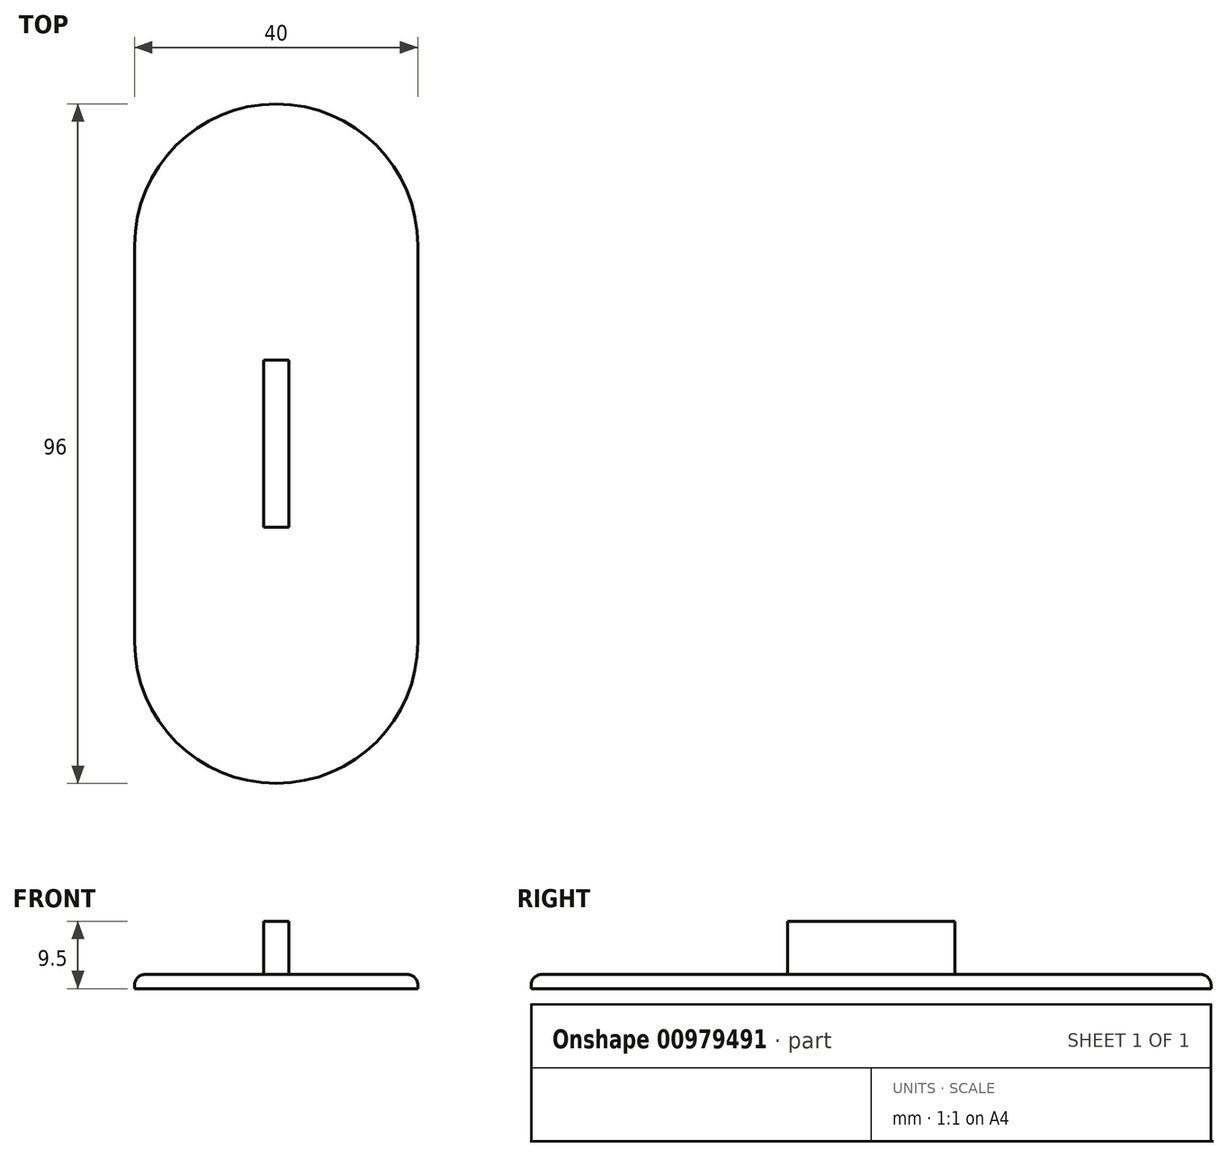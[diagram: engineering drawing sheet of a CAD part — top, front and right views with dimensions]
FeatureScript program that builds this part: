
annotation { "Feature Type Name" : "Feature", "Feature Type Description" : "" }
export const myFeature = defineFeature(function(context is Context, id is Id, definition is map)
    precondition{}
    {
        {
            assignVariable(context, id + "F0", {"name" : "MATE_DEPTH", "anyValue" : 8});
        }
        {
            var Q0;
            Q0=qCreatedBy(makeId("Top.planeOp"),FACE);
            var sketch = newSketch(context, id + "F1", { "sketchPlane" : qUnion([Q0])});
            skLineSegment(sketch, "E0.bottom", {"start": v(0, 0) * mm, "end": v(-5, 0) * mm});
            skLineSegment(sketch, "E0.top", {"start": v(0, 28) * mm, "end": v(-5, 28) * mm});
            skLineSegment(sketch, "E0.left", {"start": v(0, 0) * mm, "end": v(0, 28) * mm});
            skLineSegment(sketch, "E0.right", {"start": v(-5, 0) * mm, "end": v(-5, 28) * mm});
            skLineSegment(sketch, "E1.MirrorCS", {"start": v(0, 28) * mm, "end": v(5, 28) * mm});
            skLineSegment(sketch, "E2.MirrorCS", {"start": v(5, 0) * mm, "end": v(5, 28) * mm});
            skCircle(sketch, "E3", {"center": v(0, 28) * mm, "radius": 5 * mm});
            skLineSegment(sketch, "E4.MirrorCS", {"start": v(-5, 0) * mm, "end": v(-5, -28) * mm});
            skLineSegment(sketch, "E5.MirrorCS", {"start": v(5, 0) * mm, "end": v(5, -28) * mm});
            skCircle(sketch, "E6.MirrorC", {"center": v(0, -28) * mm, "radius": 5 * mm});
            skSolve(sketch);
        }
        {
            var Q0;
            Q0 = qSketchRegion(id + "F1", true);
            extrude(context, id + "F2", {"entities" : qUnion([Q0]), "depth" : 1 * mm, "offsetDistance" : 25 * mm});
        }
        {
            var Q0;
            Q0=qCreatedBy(makeId("Top.planeOp"),FACE);
            var sketch = newSketch(context, id + "F3", { "sketchPlane" : qUnion([Q0])});
            skArc(sketch, "E7.0", {"start": v(-20, -28) * mm, "mid": v(0, -48) * mm, "end": v(20, -28) * mm});
            skLineSegment(sketch, "E7.1", {"start": v(-20, 28) * mm, "end": v(-20, -28) * mm});
            skArc(sketch, "E7.2", {"start": v(20, 28) * mm, "mid": v(0, 48) * mm, "end": v(-20, 28) * mm});
            skLineSegment(sketch, "E7.3", {"start": v(20, -28) * mm, "end": v(20, 28) * mm});
            skSolve(sketch);
        }
        {
            var Q0;
            Q0 = qSketchRegion(id + "F3", true);
            extrude(context, id + "F4", {"entities" : qUnion([Q0]), "operationType" : NewBodyOperationType.ADD, "depth" : 2 * mm, "offsetDistance" : 25 * mm});
        }
        {
            var Q0;
            Q0=makeQuery(id+"F4.opExtrude","CAP_FACE",FACE,{"disambiguationData":[OSD([sQuery(id+"F3.wireOp",EDGE,"E7.0"),sQuery(id+"F3.wireOp",EDGE,"E7.1"),sQuery(id+"F3.wireOp",EDGE,"E7.2"),sQuery(id+"F3.wireOp",EDGE,"E7.3")])],"isStart":false});
            var sketch = newSketch(context, id + "F5", { "sketchPlane" : qUnion([Q0])});
            skLineSegment(sketch, "E8.bottom", {"start": v(0, 0) * mm, "end": v(-1.8, 0) * mm});
            skLineSegment(sketch, "E8.top", {"start": v(0, 11.8) * mm, "end": v(-1.8, 11.8) * mm});
            skLineSegment(sketch, "E8.left", {"start": v(0, 0) * mm, "end": v(0, 11.8) * mm});
            skLineSegment(sketch, "E8.right", {"start": v(-1.8, 0) * mm, "end": v(-1.8, 11.8) * mm});
            skLineSegment(sketch, "E9.MirrorCS", {"start": v(0, 11.8) * mm, "end": v(1.8, 11.8) * mm});
            skLineSegment(sketch, "E10.MirrorCS", {"start": v(1.8, 0) * mm, "end": v(1.8, 11.8) * mm});
            skLineSegment(sketch, "E11.MirrorCS", {"start": v(0, 0) * mm, "end": v(1.8, 0) * mm});
            skLineSegment(sketch, "E12.MirrorCS", {"start": v(-1.8, 0) * mm, "end": v(-1.8, -11.8) * mm});
            skLineSegment(sketch, "E13.MirrorCS", {"start": v(0, -11.8) * mm, "end": v(-1.8, -11.8) * mm});
            skLineSegment(sketch, "E14.MirrorCS", {"start": v(0, -11.8) * mm, "end": v(1.8, -11.8) * mm});
            skLineSegment(sketch, "E15.MirrorCS", {"start": v(1.8, 0) * mm, "end": v(1.8, -11.8) * mm});
            skLineSegment(sketch, "E16.MirrorCS", {"start": v(0, 0) * mm, "end": v(0, -11.8) * mm});
            skSolve(sketch);
        }
        {
            var Q0;
            Q0 = qSketchRegion(id + "F5", true);
            extrude(context, id + "F6", {"entities" : qUnion([Q0]), "operationType" : NewBodyOperationType.ADD, "depth" : (getVariable(context, 'MATE_DEPTH') - 0.5) * mm, "offsetDistance" : 25 * mm});
        }
        {
            var Q0;
            Q0=makeQuery(id+"F4.opExtrude","CAP_EDGE",EDGE,{"disambiguationData":[OSD([sQuery(id+"F3.wireOp",EDGE,"E7.1")])],"isStart":false});
            fillet(context, id + "F7", {"entities" : qUnion([Q0]), "radius" : 1.5 * mm, "tangentPropagation" : true, "allowEdgeOverflow" : false});
        }
    });
